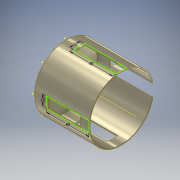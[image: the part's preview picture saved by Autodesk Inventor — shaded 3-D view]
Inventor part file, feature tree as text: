
AUTODESK INVENTOR PART (.ipt)
format: ipt  version: 2017.3 (Build 213256000, 256)  size: 198,144 bytes
history: native  units: mm
features: sketch x16, plane x10, extrude x7, fillet x1, other x1, hole x1, pattern_circular x1
ambient origin geometry x8: Origin, YZ Plane, XZ Plane, XY Plane, X Axis, Y Axis, Z Axis, Center Point
bodies: Solid1 (feature_tree)
feature tree (37):
  extrude  "Extrusion1"  Depth=53.1mm TaperAngle=0.0deg
  extrude  "Extrusion2"  Depth=52.3mm TaperAngle=0.0deg
  fillet  "Fillet1"  Radius=2.0mm
  extrude  "Extrusion3"  Depth=5.0mm TaperAngle=0.0deg
  other  "Work Axis1"
  plane  "Work Plane2"
  plane  "Work Plane4"
  sketch  "Sketch4"  dims[d10=30.3mm d11=-60.6mm d12=30.3mm d13=-60.6mm]
  sketch  "Sketch5"  dims[d14=40.0mm d15=10.0mm]
  sketch  "Sketch6"  dims[d16=30.0mm d17=10.0mm d18=40.0mm d19=10.0mm]
  sketch  "Sketch7"  dims[d20=40.0mm d21=10.0mm d26=5.0mm d27=0.0mm]
  sketch  "Sketch8"  dims[d28=5.0mm d29=0.0mm]
  sketch  "Sketch9"  dims[d30=45.0deg d31=90.0deg d32=-30.3mm d33=30.3mm d34=-30.3mm d35=30.3mm]
  sketch  "Sketch10"  dims[d71=2.0mm d72=6.0mm d73=4.0mm d74=2.0mm d75=90.0deg d76=8.0mm d77=20.594885mm d78=1.0mm d79=0.0mm]
  extrude  "Extrusion6"  Depth=30.3mm
  extrude  "Extrusion7"  Depth=10.0mm
  plane  "Work Plane5"
  plane  "Work Plane6"
  plane  "Work Plane7"
  plane  "Work Plane8"
  plane  "Work Plane9"
  plane  "Work Plane10"
  sketch  "Sketch11"  dims[d80=1.0mm d81=0.0mm d82=30.0mm d83=180.0deg]
  sketch  "Sketch12"  dims[d36=1.0mm]
  sketch  "Sketch13"  dims[d37=1.0mm]
  hole  "Hole6"  [1 undecoded]
  extrude  "Extrusion8"  Depth=10.0mm TaperAngle=0.0deg
  extrude  "Extrusion9"  Depth=1.0mm TaperAngle=0.0deg
  pattern_circular  "Circular Pattern1"  Count=3 Angle=180.0deg
  sketch  "Sketch1"  dims[d0=60.6mm d1=53.1mm d2=0.0mm]
  sketch  "Sketch2"  dims[d3=59.0mm d4=52.3mm d5=0.0mm d6=2.0mm]
  sketch  "Sketch3"  dims[d7=3.0mm d8=5.0mm d9=0.0mm]
  plane  "Work Plane1"
  plane  "Work Plane3"
  sketch  "Sketch15"
  sketch  "Sketch17"
  sketch  "Sketch18"
note: 1 required parameter value undecoded (feature->parameter linkage not recoverable at this tier; creation-order binding heuristic only, values carry confidence <= 0.55)
